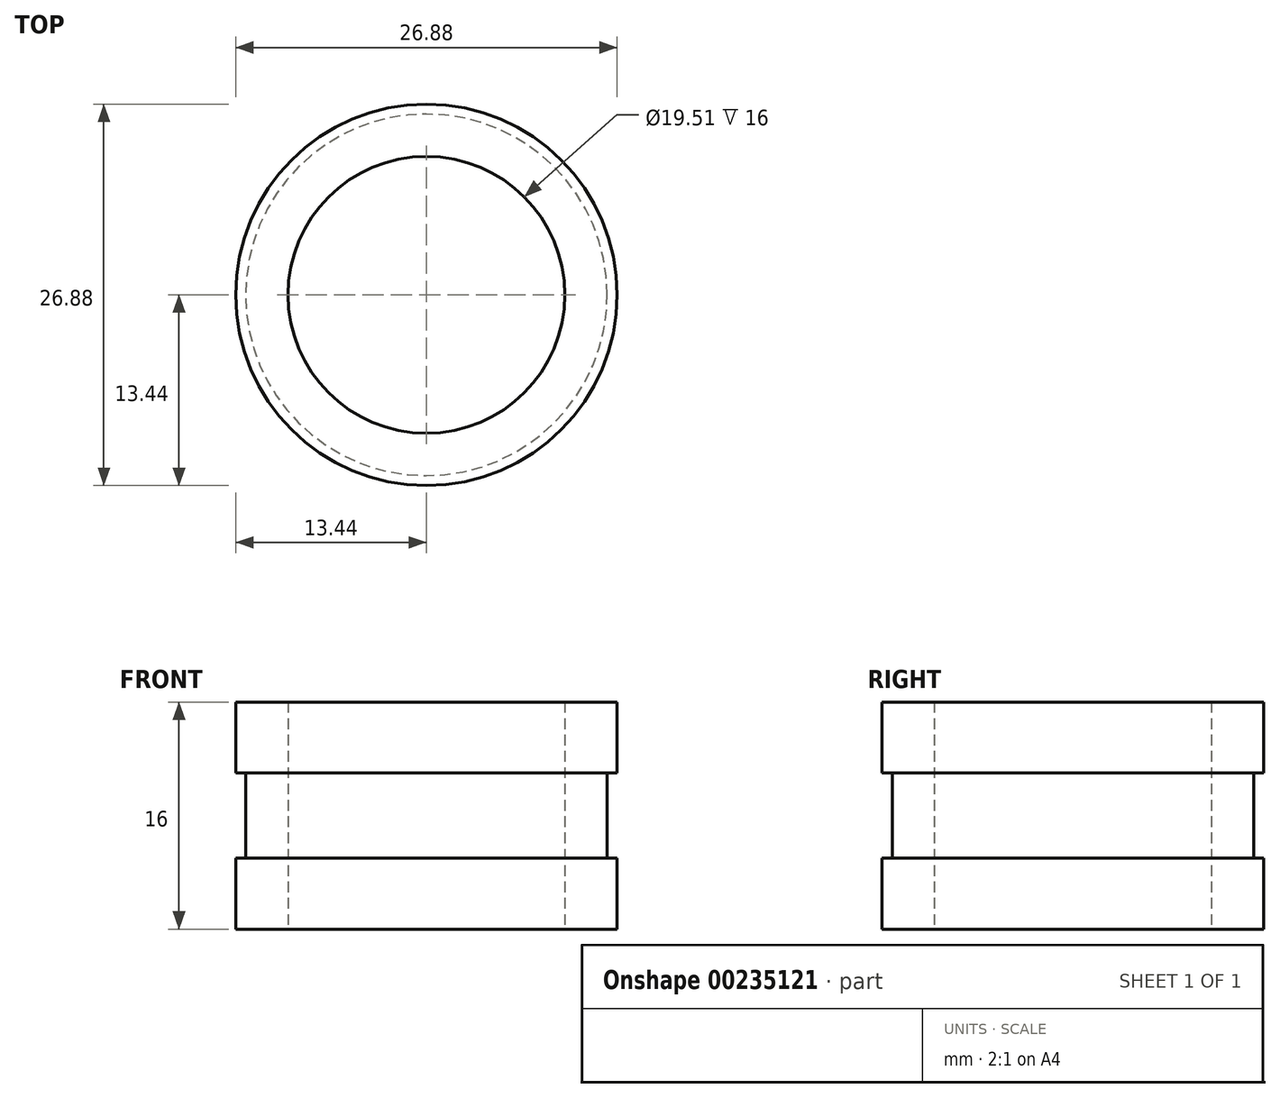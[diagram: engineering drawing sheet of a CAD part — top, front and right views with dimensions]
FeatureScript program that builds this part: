
annotation { "Feature Type Name" : "Feature", "Feature Type Description" : "" }
export const myFeature = defineFeature(function(context is Context, id is Id, definition is map)
    precondition{}
    {
        {
            var Q0;
            Q0=qCreatedBy(makeId("Top.planeOp"),FACE);
            var sketch = newSketch(context, id + "F0", { "sketchPlane" : qUnion([Q0])});
            skCircle(sketch, "E0", {"center": v(0, 0) * mm, "radius": 9.75 * mm});
            skCircle(sketch, "E1", {"center": v(0, 0) * mm, "radius": 13.44 * mm});
            skSolve(sketch);
        }
        {
            var Q0;
            Q0=makeQuery(id+"F0.imprint","IMPRINT",FACE,{"disambiguationData":[TD([[makeQuery(id+"F0.imprint","IMPRINT",EDGE,{"derivedFrom":sQuery(id+"F0.wireOp",EDGE,"E0")}),-1.0]])]});
            extrude(context, id + "F1", {"entities" : qUnion([Q0]), "endBound" : BoundingType.SYMMETRIC, "depth" : 16 * mm});
        }
        {
            var Q0;
            Q0=qCreatedBy(makeId("Top.planeOp"),FACE);
            var sketch = newSketch(context, id + "F2", { "sketchPlane" : qUnion([Q0])});
            skCircle(sketch, "E2", {"center": v(0, 0) * mm, "radius": 12.74 * mm});
            skCircle(sketch, "E3", {"center": v(0, 0) * mm, "radius": 21.65 * mm});
            skSolve(sketch);
        }
        {
            var Q0;
            Q0=makeQuery(id+"F2.imprint","IMPRINT",FACE,{"disambiguationData":[TD([[makeQuery(id+"F2.imprint","IMPRINT",EDGE,{"derivedFrom":sQuery(id+"F2.wireOp",EDGE,"E2")}),-1.0]])]});
            extrude(context, id + "F3", {"entities" : qUnion([Q0]), "operationType" : NewBodyOperationType.REMOVE, "endBound" : BoundingType.SYMMETRIC, "depth" : 6 * mm});
        }
    });
